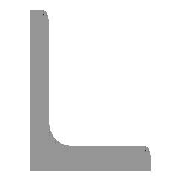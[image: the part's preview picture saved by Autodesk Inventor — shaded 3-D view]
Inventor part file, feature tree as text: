
AUTODESK INVENTOR PART (.ipt)
format: ipt  version: 2013 (Build 170138000, 138)  size: 129,536 bytes
history: native  units: mm (DEFAULTED — no unit token found)
features: other x4, plane x3, split x2, sketch x2
ambient origin geometry x8: Origin, YZ Plane, XZ Plane, XY Plane, X Axis, Y Axis, Z Axis, Center Point
bodies: Solid1 (feature_tree), Body (feature_tree)
feature tree (11):
  parser-record x1  (decoder bookkeeping rows leaked as tree rows — omitted from the tree; the rows remain in map.json)
  other  "Driven Length"
  other  "Start plane"
  other  "End plane"
  plane  "Work Plane4"
  split  "Split1"
  plane  "Work Plane5"
  split  "Split2"
  sketch  "Sketch3"  dims[d0=38.1mm]
  plane  "Work Plane3"
  sketch  "Sketch4"  dims[d1=38.1mm d2=4.7625mm d3=4.7625mm d4=1054.1mm d5=0.0mm d10=0.0mm d11=0.0mm d12=-0.0mm d13=1054.1mm d14=4.826mm d15=2.286mm d16=90.0deg d17=1054.1mm]
